# Revit family: FU_Bench_Sandler_Plania_PL90904
name_source: partatom
category: Furniture
units: mm (PartAtom-declared; Revit-internal decimal feet)

## family parameters
Always vertical = Yes
Cut with Voids When Loaded = No
OmniClass Number = 23.40.20.00
OmniClass Title = General Furniture and Specialties
Room Calculation Point = No
Shared = No
Work Plane-Based = No

## types (1)
- PL90904
    Default Elevation = 0 mm  [stored 0 ft]
    Depth = 710 mm  [stored 2.3294 ft]
    Elevation = 420 mm  [stored 1.37795 ft]
    Frame Finish = Epoxy - M1_B00 - Black
    Manufacturer = Sandler
    Model = PL90904
    Top Finish = Wood - Oak - Walnut
    Type Comments = Plania connecting Top (4 ways 90°)
    URL = https://www.sandlerseating.com
    Width = 710 mm  [stored 2.3294 ft]

note: [stored X ft] marks values corroborated as IEEE doubles in the binary element streams (Revit-internal decimal feet)

## geometry (parser evidence)
native form markers: Sweep x3
no freeform markers — native parametric forms only
